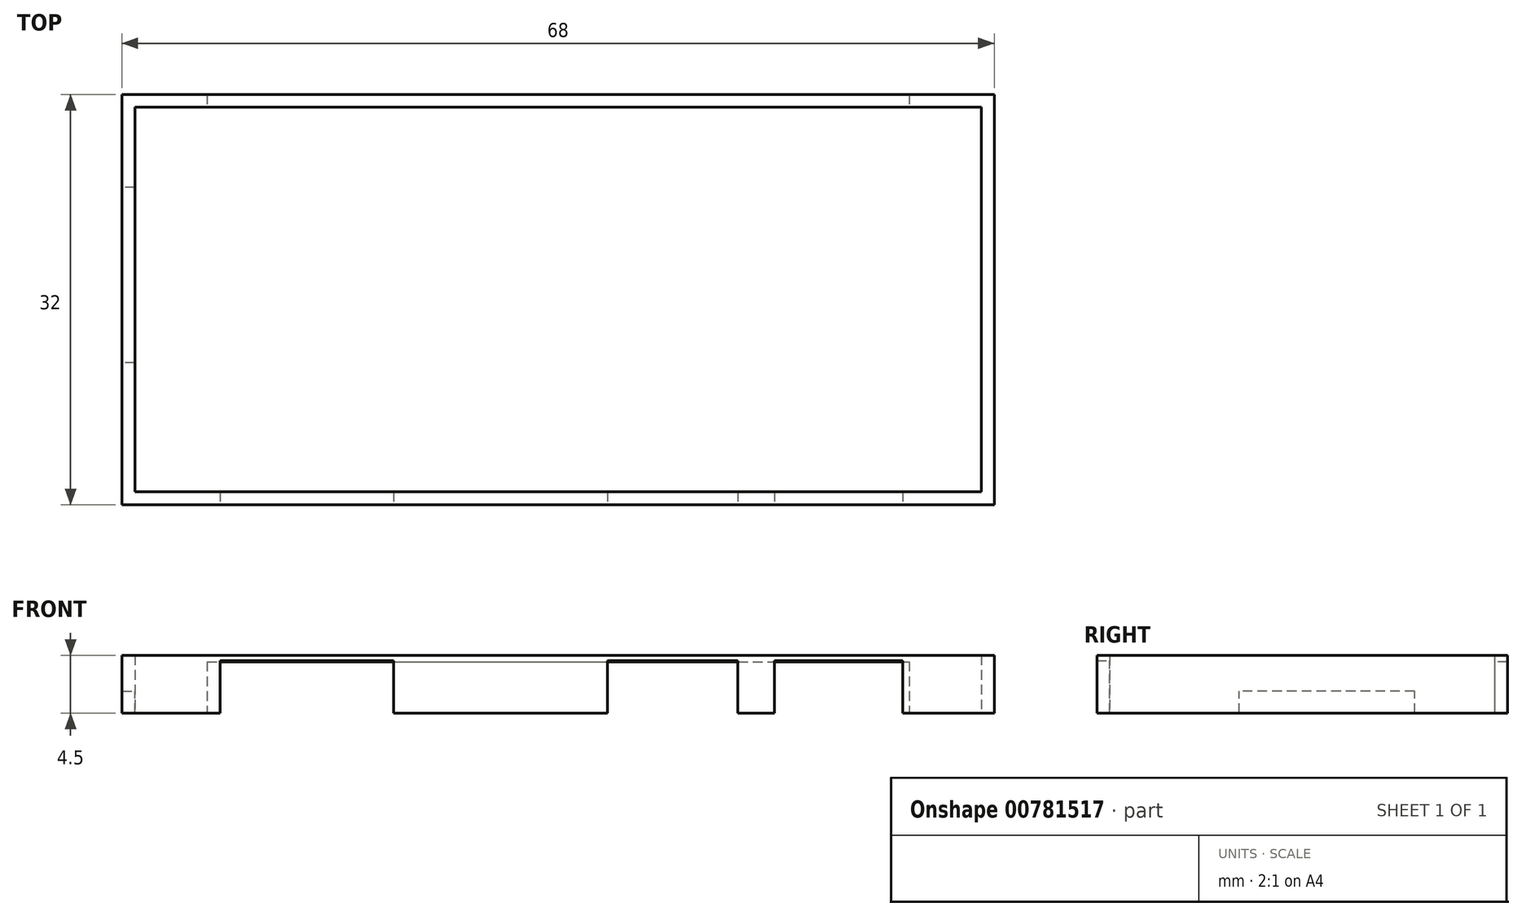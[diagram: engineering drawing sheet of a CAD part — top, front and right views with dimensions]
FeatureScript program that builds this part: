
annotation { "Feature Type Name" : "Feature", "Feature Type Description" : "" }
export const myFeature = defineFeature(function(context is Context, id is Id, definition is map)
    precondition{}
    {
        {
            var Q0;
            Q0=qCreatedBy(makeId("Top.planeOp"),FACE);
            var sketch = newSketch(context, id + "F0", { "sketchPlane" : qUnion([Q0])});
            skLineSegment(sketch, "E0.bottom", {"start": v(-34, 15.91) * mm, "end": v(34, 15.91) * mm});
            skLineSegment(sketch, "E0.top", {"start": v(-34, -16.09) * mm, "end": v(34, -16.09) * mm});
            skLineSegment(sketch, "E0.left", {"start": v(-34, 15.91) * mm, "end": v(-34, -16.09) * mm});
            skLineSegment(sketch, "E0.right", {"start": v(34, 15.91) * mm, "end": v(34, -16.09) * mm});
            skLineSegment(sketch, "E1.bottom", {"start": v(-33, 14.91) * mm, "end": v(33, 14.91) * mm});
            skLineSegment(sketch, "E1.top", {"start": v(-33, -15.09) * mm, "end": v(33, -15.09) * mm});
            skLineSegment(sketch, "E1.left", {"start": v(-33, 14.91) * mm, "end": v(-33, -15.09) * mm});
            skLineSegment(sketch, "E1.right", {"start": v(33, 14.91) * mm, "end": v(33, -15.09) * mm});
            skPoint(sketch, "E2", {"position": v(0, -15.09) * mm});
            skPoint(sketch, "E3", {"position": v(0, -16.09) * mm});
            skPoint(sketch, "E4", {"position": v(0, 14.91) * mm});
            skPoint(sketch, "E5", {"position": v(0, 15.91) * mm});
            skPoint(sketch, "E6", {"position": v(-34, -0.09) * mm});
            skPoint(sketch, "E7", {"position": v(-33, -0.09) * mm});
            skPoint(sketch, "E8", {"position": v(33, -0.09) * mm});
            skPoint(sketch, "E9", {"position": v(34, -0.09) * mm});
            skSolve(sketch);
        }
        {
            var Q0;
            Q0=qCreatedBy(makeId("Top.planeOp"),FACE);
            var sketch = newSketch(context, id + "F1", { "sketchPlane" : qUnion([Q0])});
            skLineSegment(sketch, "E10.bottom", {"start": v(-26.34, -17.54) * mm, "end": v(-12.84, -17.54) * mm});
            skLineSegment(sketch, "E10.top", {"start": v(-26.34, -9.55) * mm, "end": v(-12.84, -9.55) * mm});
            skLineSegment(sketch, "E10.left", {"start": v(-26.34, -17.54) * mm, "end": v(-26.34, -9.55) * mm});
            skLineSegment(sketch, "E10.right", {"start": v(-12.84, -17.54) * mm, "end": v(-12.84, -9.55) * mm});
            skLineSegment(sketch, "E11.bottom", {"start": v(3.84, -17.54) * mm, "end": v(14.02, -17.54) * mm});
            skLineSegment(sketch, "E11.top", {"start": v(3.84, -9.55) * mm, "end": v(14.02, -9.55) * mm});
            skLineSegment(sketch, "E11.left", {"start": v(3.84, -17.54) * mm, "end": v(3.84, -9.55) * mm});
            skLineSegment(sketch, "E11.right", {"start": v(14.02, -17.54) * mm, "end": v(14.02, -9.55) * mm});
            skLineSegment(sketch, "E12.bottom", {"start": v(16.87, -17.41) * mm, "end": v(26.88, -17.41) * mm});
            skLineSegment(sketch, "E12.top", {"start": v(16.87, -9.55) * mm, "end": v(26.88, -9.55) * mm});
            skLineSegment(sketch, "E12.left", {"start": v(16.87, -17.41) * mm, "end": v(16.87, -9.55) * mm});
            skLineSegment(sketch, "E12.right", {"start": v(26.88, -17.41) * mm, "end": v(26.88, -9.55) * mm});
            skSolve(sketch);
        }
        {
            var Q0;
            Q0=qSketchRegion(id+"F0",true);
            extrude(context, id + "F2", {"entities" : qUnion([Q0]), "depth" : 6 * mm, "offsetDistance" : 25 * mm, "hasSecondDirection" : true, "secondDirectionOppositeDirection" : false, "secondDirectionDepth" : 1.5 * mm});
        }
        {
            var Q0;
            Q0=qCreatedBy(makeId("Top.planeOp"),FACE);
            var sketch = newSketch(context, id + "F3", { "sketchPlane" : qUnion([Q0])});
            skLineSegment(sketch, "E13.bottom", {"start": v(-35.27, 8.67) * mm, "end": v(-25.56, 8.67) * mm});
            skLineSegment(sketch, "E13.top", {"start": v(-35.27, -5) * mm, "end": v(-25.56, -5) * mm});
            skLineSegment(sketch, "E13.left", {"start": v(-35.27, 8.67) * mm, "end": v(-35.27, -5) * mm});
            skLineSegment(sketch, "E13.right", {"start": v(-25.56, 8.67) * mm, "end": v(-25.56, -5) * mm});
            skSolve(sketch);
        }
        {
            var Q0;
            Q0=qCreatedBy(makeId("Top.planeOp"),FACE);
            var sketch = newSketch(context, id + "F4", { "sketchPlane" : qUnion([Q0])});
            skLineSegment(sketch, "E14.bottom", {"start": v(-27.35, 17.47) * mm, "end": v(27.37, 17.47) * mm});
            skLineSegment(sketch, "E14.top", {"start": v(-27.35, 9.27) * mm, "end": v(27.37, 9.27) * mm});
            skLineSegment(sketch, "E14.left", {"start": v(-27.35, 17.47) * mm, "end": v(-27.35, 9.27) * mm});
            skLineSegment(sketch, "E14.right", {"start": v(27.37, 17.47) * mm, "end": v(27.37, 9.27) * mm});
            skSolve(sketch);
        }
        {
            var Q0;
            Q0=qSketchRegion(id+"F3",true);
            extrude(context, id + "F5", {"entities" : qUnion([Q0]), "operationType" : NewBodyOperationType.REMOVE, "depth" : 3.2 * mm, "offsetDistance" : 25 * mm, "hasSecondDirection" : true, "secondDirectionOppositeDirection" : false, "secondDirectionDepth" : 0.9 * mm});
        }
        {
            var Q0;
            Q0=qSketchRegion(id+"F1",true);
            extrude(context, id + "F6", {"entities" : qUnion([Q0]), "operationType" : NewBodyOperationType.REMOVE, "depth" : 5.6 * mm, "offsetDistance" : 25 * mm, "hasSecondDirection" : true, "secondDirectionOppositeDirection" : false, "secondDirectionDepth" : 1 * mm});
        }
        {
            var Q0;
            Q0=qSketchRegion(id+"F4",true);
            extrude(context, id + "F7", {"entities" : qUnion([Q0]), "operationType" : NewBodyOperationType.REMOVE, "depth" : 5.5 * mm, "offsetDistance" : 25 * mm, "hasSecondDirection" : true, "secondDirectionOppositeDirection" : false, "secondDirectionDepth" : 1.5 * mm});
        }
    });
